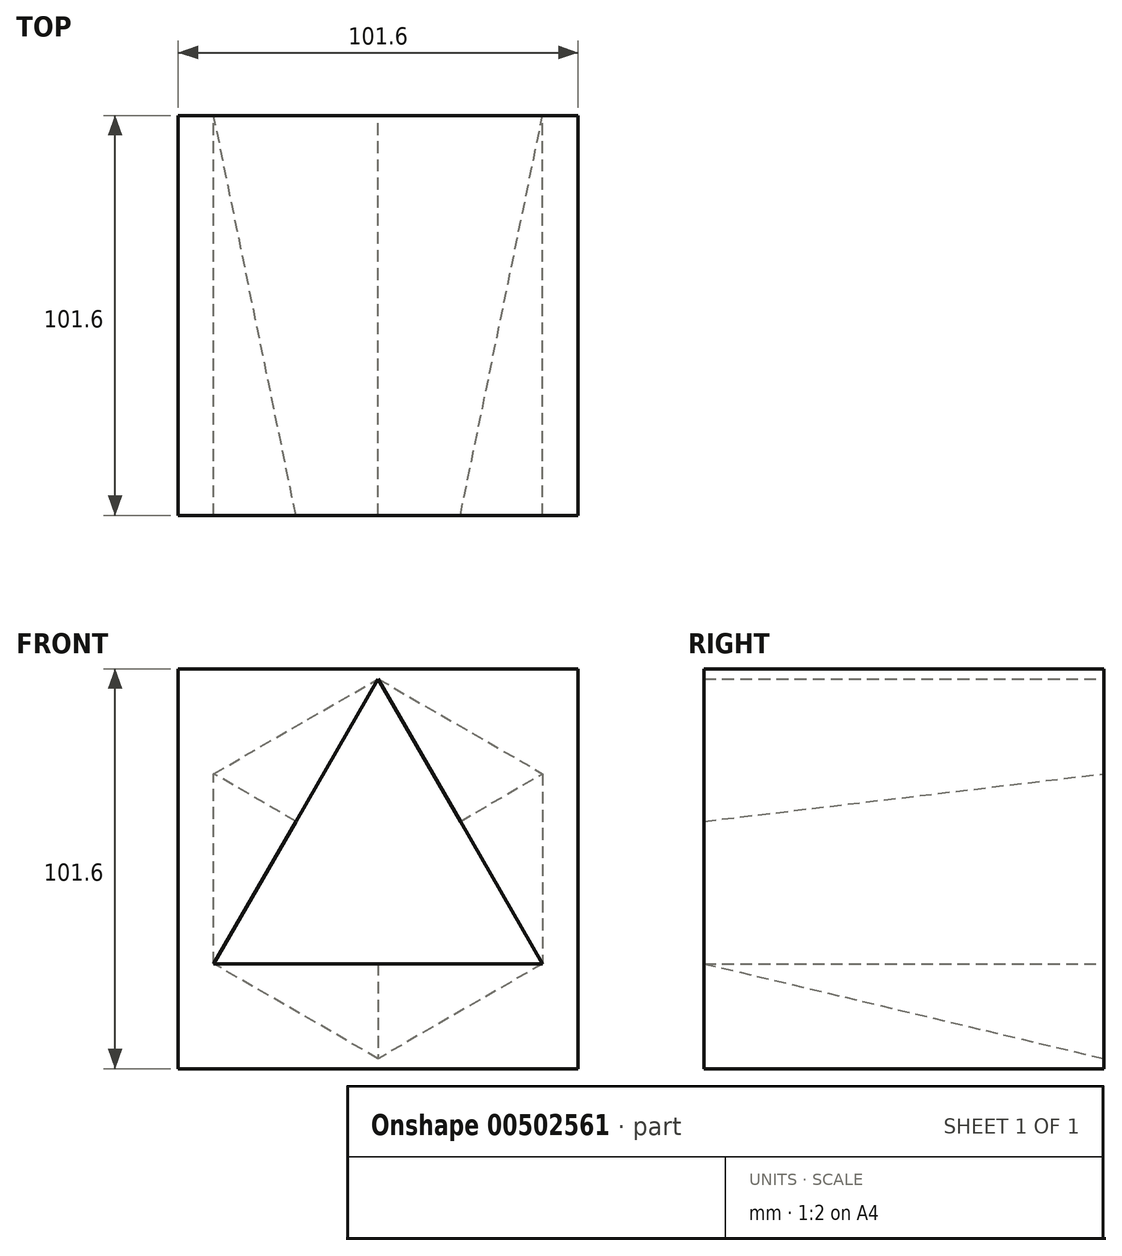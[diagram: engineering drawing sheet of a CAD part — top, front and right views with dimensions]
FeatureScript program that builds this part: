
annotation { "Feature Type Name" : "Feature", "Feature Type Description" : "" }
export const myFeature = defineFeature(function(context is Context, id is Id, definition is map)
    precondition{}
    {
        {
            var Q0;
            Q0=qCreatedBy(makeId("Front.planeOp"),FACE);
            var sketch = newSketch(context, id + "F0", { "sketchPlane" : qUnion([Q0])});
            skLineSegment(sketch, "E0.bottom", {"start": v(50.8, 50.8) * mm, "end": v(-50.8, 50.8) * mm});
            skLineSegment(sketch, "E0.top", {"start": v(50.8, -50.8) * mm, "end": v(-50.8, -50.8) * mm});
            skLineSegment(sketch, "E0.left", {"start": v(50.8, 50.8) * mm, "end": v(50.8, -50.8) * mm});
            skLineSegment(sketch, "E0.right", {"start": v(-50.8, 50.8) * mm, "end": v(-50.8, -50.8) * mm});
            skPoint(sketch, "E0.middle", {"position": v(0, 0) * mm});
            skSolve(sketch);
        }
        {
            var Q0;
            Q0=makeQuery(id+"F0.imprint","IMPRINT",FACE,{"disambiguationData":[TD([[makeQuery(id+"F0.imprint","IMPRINT",EDGE,{"derivedFrom":sQuery(id+"F0.wireOp",EDGE,"E0.bottom")}),1.0]])]});
            extrude(context, id + "F1", {"entities" : qUnion([Q0]), "depth" : 101.6 * mm});
        }
        {
            var Q0;
            Q0=qCreatedBy(makeId("Front.planeOp"),FACE);
            var sketch = newSketch(context, id + "F2", { "sketchPlane" : qUnion([Q0])});
            skCircle(sketch, "E1.cCircle", {"center": v(0, 0) * mm, "radius": 48.25 * mm, "construction": true});
            skLineSegment(sketch, "E1.0", {"start": v(0, 48.25) * mm, "end": v(41.78, 24.12) * mm});
            skLineSegment(sketch, "E1.1", {"start": v(41.78, 24.12) * mm, "end": v(41.78, -24.12) * mm});
            skLineSegment(sketch, "E1.2", {"start": v(41.78, -24.12) * mm, "end": v(0, -48.25) * mm});
            skLineSegment(sketch, "E1.3", {"start": v(0, -48.25) * mm, "end": v(-41.78, -24.12) * mm});
            skLineSegment(sketch, "E1.4", {"start": v(-41.78, -24.12) * mm, "end": v(-41.78, 24.12) * mm});
            skLineSegment(sketch, "E1.5", {"start": v(-41.78, 24.12) * mm, "end": v(0, 48.25) * mm});
            skSolve(sketch);
        }
        {
            var Q0;
            Q0=makeQuery(id+"F1.opExtrude","CAP_FACE",FACE,{"disambiguationData":[OSD([sQuery(id+"F0.wireOp",EDGE,"E0.bottom"),sQuery(id+"F0.wireOp",EDGE,"E0.top"),sQuery(id+"F0.wireOp",EDGE,"E0.left"),sQuery(id+"F0.wireOp",EDGE,"E0.right")])],"isStart":false});
            var sketch = newSketch(context, id + "F3", { "sketchPlane" : qUnion([Q0])});
            skCircle(sketch, "E2.cCircle", {"center": v(0, 0) * mm, "radius": 48.25 * mm, "construction": true});
            skLineSegment(sketch, "E2.0", {"start": v(0, 48.25) * mm, "end": v(41.78, -24.12) * mm});
            skLineSegment(sketch, "E2.1", {"start": v(41.78, -24.12) * mm, "end": v(-41.78, -24.12) * mm});
            skLineSegment(sketch, "E2.2", {"start": v(-41.78, -24.12) * mm, "end": v(0, 48.25) * mm});
            skSolve(sketch);
        }
        {
            var Q1;
            Q1=makeQuery(id+"F3.imprint","IMPRINT",FACE,{"disambiguationData":[TD([[makeQuery(id+"F3.imprint","IMPRINT",EDGE,{"derivedFrom":sQuery(id+"F3.wireOp",EDGE,"E2.0")}),-1.0]])]});
            var Q2;
            Q2=makeQuery(id+"F2.imprint","IMPRINT",FACE,{"disambiguationData":[TD([[makeQuery(id+"F2.imprint","IMPRINT",EDGE,{"derivedFrom":sQuery(id+"F2.wireOp",EDGE,"E1.0")}),-1.0]])]});
            loft(context, id + "F4", {"operationType" : NewBodyOperationType.REMOVE, "sheetProfilesArray" : [{ "sheetProfileEntities" : qUnion([Q1]) }, { "sheetProfileEntities" : qUnion([Q2]) }]});
        }
    });
